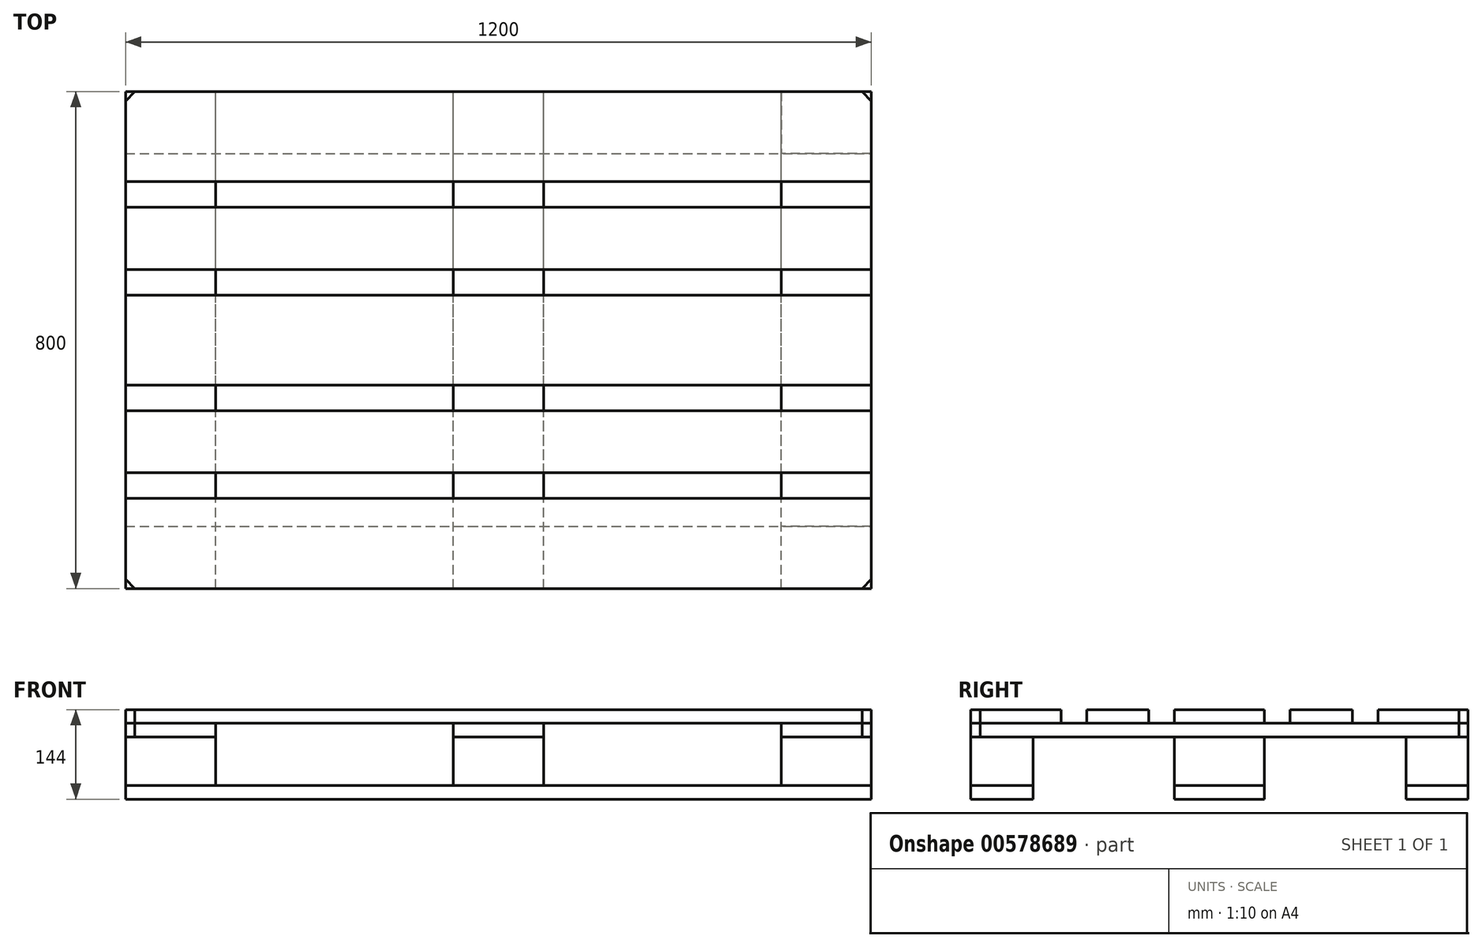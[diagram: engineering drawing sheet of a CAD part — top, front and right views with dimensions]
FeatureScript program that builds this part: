
annotation { "Feature Type Name" : "Feature", "Feature Type Description" : "" }
export const myFeature = defineFeature(function(context is Context, id is Id, definition is map)
    precondition{}
    {
        {
            var Q0;
            Q0=qCreatedBy(makeId("Top.planeOp"),FACE);
            var sketch = newSketch(context, id + "F0", { "sketchPlane" : qUnion([Q0])});
            skLineSegment(sketch, "E0.bottom", {"start": v(600, -72.5) * mm, "end": v(-600, -72.5) * mm});
            skLineSegment(sketch, "E0.top", {"start": v(600, 72.5) * mm, "end": v(-600, 72.5) * mm});
            skLineSegment(sketch, "E0.left", {"start": v(600, -72.5) * mm, "end": v(600, 72.5) * mm});
            skLineSegment(sketch, "E0.right", {"start": v(-600, -72.5) * mm, "end": v(-600, 72.5) * mm});
            skPoint(sketch, "E0.middle", {"position": v(0, 0) * mm});
            skLineSegment(sketch, "E1.bottom", {"start": v(600, -213.75) * mm, "end": v(-600, -213.75) * mm});
            skLineSegment(sketch, "E1.top", {"start": v(600, -113.75) * mm, "end": v(-600, -113.75) * mm});
            skLineSegment(sketch, "E1.left", {"start": v(600, -213.75) * mm, "end": v(600, -113.75) * mm});
            skLineSegment(sketch, "E1.right", {"start": v(-600, -213.75) * mm, "end": v(-600, -113.75) * mm});
            skPoint(sketch, "E1.middle", {"position": v(0, -163.75) * mm});
            skLineSegment(sketch, "E2.bottom", {"start": v(600, -400) * mm, "end": v(-600, -400) * mm});
            skLineSegment(sketch, "E2.top", {"start": v(600, -255) * mm, "end": v(-600, -255) * mm});
            skLineSegment(sketch, "E2.left", {"start": v(600, -400) * mm, "end": v(600, -255) * mm});
            skLineSegment(sketch, "E2.right", {"start": v(-600, -400) * mm, "end": v(-600, -255) * mm});
            skPoint(sketch, "E2.middle", {"position": v(0, -327.5) * mm});
            skLineSegment(sketch, "E3.bottom", {"start": v(-600, 213.75) * mm, "end": v(600, 213.75) * mm});
            skLineSegment(sketch, "E3.top", {"start": v(-600, 113.75) * mm, "end": v(600, 113.75) * mm});
            skLineSegment(sketch, "E3.left", {"start": v(-600, 213.75) * mm, "end": v(-600, 113.75) * mm});
            skLineSegment(sketch, "E3.right", {"start": v(600, 213.75) * mm, "end": v(600, 113.75) * mm});
            skPoint(sketch, "E3.middle", {"position": v(0, 163.75) * mm});
            skLineSegment(sketch, "E4.bottom", {"start": v(-600, 400) * mm, "end": v(600, 400) * mm});
            skLineSegment(sketch, "E4.top", {"start": v(-600, 255) * mm, "end": v(600, 255) * mm});
            skLineSegment(sketch, "E4.left", {"start": v(-600, 400) * mm, "end": v(-600, 255) * mm});
            skLineSegment(sketch, "E4.right", {"start": v(600, 400) * mm, "end": v(600, 255) * mm});
            skPoint(sketch, "E4.middle", {"position": v(0, 327.5) * mm});
            skLineSegment(sketch, "E5", {"start": v(-600, 163.75) * mm, "end": v(600, 163.75) * mm, "construction": true});
            skSolve(sketch);
        }
        {
            var Q0;
            Q0=makeQuery(id+"F0.imprint","IMPRINT",FACE,{"disambiguationData":[TD([[makeQuery(id+"F0.imprint","IMPRINT",EDGE,{"derivedFrom":sQuery(id+"F0.wireOp",EDGE,"E4.bottom")}),-1.0]])]});
            var Q1;
            Q1=makeQuery(id+"F0.imprint","IMPRINT",FACE,{"disambiguationData":[TD([[makeQuery(id+"F0.imprint","IMPRINT",EDGE,{"derivedFrom":sQuery(id+"F0.wireOp",EDGE,"E3.bottom")}),-1.0]])]});
            var Q2;
            Q2=makeQuery(id+"F0.imprint","IMPRINT",FACE,{"disambiguationData":[TD([[makeQuery(id+"F0.imprint","IMPRINT",EDGE,{"derivedFrom":sQuery(id+"F0.wireOp",EDGE,"E0.bottom")}),-1.0]])]});
            var Q3;
            Q3=makeQuery(id+"F0.imprint","IMPRINT",FACE,{"disambiguationData":[TD([[makeQuery(id+"F0.imprint","IMPRINT",EDGE,{"derivedFrom":sQuery(id+"F0.wireOp",EDGE,"E1.bottom")}),-1.0]])]});
            var Q4;
            Q4=makeQuery(id+"F0.imprint","IMPRINT",FACE,{"disambiguationData":[TD([[makeQuery(id+"F0.imprint","IMPRINT",EDGE,{"derivedFrom":sQuery(id+"F0.wireOp",EDGE,"E2.bottom")}),-1.0]])]});
            extrude(context, id + "F1", {"entities" : qUnion([Q0, Q1, Q2, Q3, Q4]), "oppositeDirection" : true, "depth" : 22 * mm, "offsetDistance" : 25 * mm});
        }
        {
            var Q0;
            Q0=makeQuery(id+"F1.opExtrude","CAP_FACE",FACE,{"disambiguationData":[OSD([sQuery(id+"F0.wireOp",EDGE,"E2.bottom"),sQuery(id+"F0.wireOp",EDGE,"E2.top"),sQuery(id+"F0.wireOp",EDGE,"E2.left"),sQuery(id+"F0.wireOp",EDGE,"E2.right")])],"isStart":false});
            var sketch = newSketch(context, id + "F2", { "sketchPlane" : qUnion([Q0])});
            skLineSegment(sketch, "E6.bottom", {"start": v(-600, 400) * mm, "end": v(-455, 400) * mm});
            skLineSegment(sketch, "E6.top", {"start": v(-600, -400) * mm, "end": v(-455, -400) * mm});
            skLineSegment(sketch, "E6.left", {"start": v(-600, 400) * mm, "end": v(-600, -400) * mm});
            skLineSegment(sketch, "E6.right", {"start": v(-455, 400) * mm, "end": v(-455, -400) * mm});
            skLineSegment(sketch, "E7.bottom", {"start": v(-72.5, 400) * mm, "end": v(72.5, 400) * mm});
            skLineSegment(sketch, "E7.top", {"start": v(-72.5, -400) * mm, "end": v(72.5, -400) * mm});
            skLineSegment(sketch, "E7.left", {"start": v(-72.5, 400) * mm, "end": v(-72.5, -400) * mm});
            skLineSegment(sketch, "E7.right", {"start": v(72.5, 400) * mm, "end": v(72.5, -400) * mm});
            skLineSegment(sketch, "E8.bottom", {"start": v(600, 400) * mm, "end": v(455, 400) * mm});
            skLineSegment(sketch, "E8.top", {"start": v(600, -400) * mm, "end": v(455, -400) * mm});
            skLineSegment(sketch, "E8.left", {"start": v(600, 400) * mm, "end": v(600, -400) * mm});
            skLineSegment(sketch, "E8.right", {"start": v(455, 400) * mm, "end": v(455, -400) * mm});
            skSolve(sketch);
        }
        {
            var Q0;
            {var subQ0=sQuery(id+"F2.wireOp",EDGE,"E6.top");Q0=makeQuery(id+"F2.imprint","IMPRINT",FACE,{"disambiguationData":[TD([[makeQuery(id+"F2.imprint","IMPRINT",EDGE,{"derivedFrom":subQ0}),1.0]])]});}
            var Q1;
            {var subQ0=sQuery(id+"F2.wireOp",EDGE,"E6.bottom");Q1=makeQuery(id+"F2.imprint","IMPRINT",FACE,{"disambiguationData":[TD([[makeQuery(id+"F2.imprint","IMPRINT",EDGE,{"derivedFrom":subQ0}),1.0]])]});}
            var Q2;
            {var subQ0=sQuery(id+"F2.wireOp",EDGE,"E7.bottom");Q2=makeQuery(id+"F2.imprint","IMPRINT",FACE,{"disambiguationData":[TD([[makeQuery(id+"F2.imprint","IMPRINT",EDGE,{"derivedFrom":subQ0}),1.0]])]});}
            var Q3;
            {var subQ0=sQuery(id+"F2.wireOp",EDGE,"E7.top");Q3=makeQuery(id+"F2.imprint","IMPRINT",FACE,{"disambiguationData":[TD([[makeQuery(id+"F2.imprint","IMPRINT",EDGE,{"derivedFrom":subQ0}),1.0]])]});}
            var Q4;
            {var subQ0=sQuery(id+"F2.wireOp",EDGE,"E8.bottom");Q4=makeQuery(id+"F2.imprint","IMPRINT",FACE,{"disambiguationData":[TD([[makeQuery(id+"F2.imprint","IMPRINT",EDGE,{"derivedFrom":subQ0}),1.0]])]});}
            var Q5;
            {var subQ0=sQuery(id+"F2.wireOp",EDGE,"E8.top");Q5=makeQuery(id+"F2.imprint","IMPRINT",FACE,{"disambiguationData":[TD([[makeQuery(id+"F2.imprint","IMPRINT",EDGE,{"derivedFrom":subQ0}),-1.0]])]});}
            extrude(context, id + "F3", {"entities" : qUnion([Q0, Q1, Q2, Q3, Q4, Q5]), "depth" : 22 * mm, "offsetDistance" : 25 * mm});
        }
        {
            var Q0;
            Q0=makeQuery(id+"F3.opExtrude","CAP_FACE",FACE,{"disambiguationData":[OSD([sQuery(id+"F2.wireOp",EDGE,"E6.bottom"),sQuery(id+"F2.wireOp",EDGE,"E6.top"),sQuery(id+"F2.wireOp",EDGE,"E6.left"),sQuery(id+"F2.wireOp",EDGE,"E6.right")])],"isStart":false});
            var sketch = newSketch(context, id + "F4", { "sketchPlane" : qUnion([Q0])});
            skLineSegment(sketch, "E9.bottom", {"start": v(-600, -400) * mm, "end": v(-455, -400) * mm});
            skLineSegment(sketch, "E9.top", {"start": v(-600, -300) * mm, "end": v(-455, -300) * mm});
            skLineSegment(sketch, "E9.left", {"start": v(-600, -400) * mm, "end": v(-600, -300) * mm});
            skLineSegment(sketch, "E9.right", {"start": v(-455, -400) * mm, "end": v(-455, -300) * mm});
            skLineSegment(sketch, "E10", {"start": v(-600, 0) * mm, "end": v(600, 0) * mm, "construction": true});
            skPoint(sketch, "E10.endSnap0", {"position": v(-600, 0) * mm});
            skLineSegment(sketch, "E11", {"start": v(0, 0) * mm, "end": v(0, 291.88) * mm, "construction": true});
            skLineSegment(sketch, "E12.MirrorCS", {"start": v(-600, 300) * mm, "end": v(-455, 300) * mm});
            skLineSegment(sketch, "E13.MirrorCS", {"start": v(-455, 400) * mm, "end": v(-455, 300) * mm});
            skLineSegment(sketch, "E14.MirrorCS", {"start": v(-600, 400) * mm, "end": v(-455, 400) * mm});
            skLineSegment(sketch, "E15.MirrorCS", {"start": v(-600, 400) * mm, "end": v(-600, 300) * mm});
            skLineSegment(sketch, "E16.bottom", {"start": v(-600, -72.5) * mm, "end": v(-455, -72.5) * mm});
            skLineSegment(sketch, "E16.top", {"start": v(-600, 72.5) * mm, "end": v(-455, 72.5) * mm});
            skLineSegment(sketch, "E16.left", {"start": v(-600, -72.5) * mm, "end": v(-600, 72.5) * mm});
            skLineSegment(sketch, "E16.right", {"start": v(-455, -72.5) * mm, "end": v(-455, 72.5) * mm});
            skPoint(sketch, "E17.MirrorP", {"position": v(600, 0) * mm});
            skLineSegment(sketch, "E18.MirrorCS", {"start": v(455, -72.5) * mm, "end": v(455, 72.5) * mm});
            skLineSegment(sketch, "E19.MirrorCS", {"start": v(600, -400) * mm, "end": v(455, -400) * mm});
            skLineSegment(sketch, "E20.MirrorCS", {"start": v(600, 400) * mm, "end": v(455, 400) * mm});
            skLineSegment(sketch, "E21.MirrorCS", {"start": v(600, -400) * mm, "end": v(600, -300) * mm});
            skLineSegment(sketch, "E22.MirrorCS", {"start": v(455, 400) * mm, "end": v(455, 300) * mm});
            skLineSegment(sketch, "E23.MirrorCS", {"start": v(600, -72.5) * mm, "end": v(455, -72.5) * mm});
            skLineSegment(sketch, "E24.MirrorCS", {"start": v(455, -400) * mm, "end": v(455, -300) * mm});
            skLineSegment(sketch, "E25.MirrorCS", {"start": v(600, 72.5) * mm, "end": v(455, 72.5) * mm});
            skLineSegment(sketch, "E26.MirrorCS", {"start": v(600, 400) * mm, "end": v(600, 300) * mm});
            skLineSegment(sketch, "E27.MirrorCS", {"start": v(600, -72.5) * mm, "end": v(600, 72.5) * mm});
            skLineSegment(sketch, "E28.MirrorCS", {"start": v(600, -300) * mm, "end": v(455, -300) * mm});
            skLineSegment(sketch, "E29.MirrorCS", {"start": v(600, 300) * mm, "end": v(455, 300) * mm});
            skPoint(sketch, "E30", {"position": v(0, 0) * mm});
            skSolve(sketch);
        }
        {
            var Q0;
            Q0=makeQuery(id+"F3.opExtrude","CAP_FACE",FACE,{"disambiguationData":[OSD([sQuery(id+"F2.wireOp",EDGE,"E7.bottom"),sQuery(id+"F2.wireOp",EDGE,"E7.top"),sQuery(id+"F2.wireOp",EDGE,"E7.left"),sQuery(id+"F2.wireOp",EDGE,"E7.right")])],"isStart":false});
            var sketch = newSketch(context, id + "F5", { "sketchPlane" : qUnion([Q0])});
            skLineSegment(sketch, "E31.bottom", {"start": v(-72.5, -400) * mm, "end": v(72.5, -400) * mm});
            skLineSegment(sketch, "E31.top", {"start": v(-72.5, -300) * mm, "end": v(72.5, -300) * mm});
            skLineSegment(sketch, "E31.left", {"start": v(-72.5, -400) * mm, "end": v(-72.5, -300) * mm});
            skLineSegment(sketch, "E31.right", {"start": v(72.5, -400) * mm, "end": v(72.5, -300) * mm});
            skLineSegment(sketch, "E32.bottom", {"start": v(-72.5, 400) * mm, "end": v(72.5, 400) * mm});
            skLineSegment(sketch, "E32.top", {"start": v(-72.5, 300) * mm, "end": v(72.5, 300) * mm});
            skLineSegment(sketch, "E32.left", {"start": v(-72.5, 400) * mm, "end": v(-72.5, 300) * mm});
            skLineSegment(sketch, "E32.right", {"start": v(72.5, 400) * mm, "end": v(72.5, 300) * mm});
            skLineSegment(sketch, "E33.bottom", {"start": v(-72.5, 72.5) * mm, "end": v(72.5, 72.5) * mm});
            skLineSegment(sketch, "E33.top", {"start": v(-72.5, -72.5) * mm, "end": v(72.5, -72.5) * mm});
            skLineSegment(sketch, "E33.left", {"start": v(-72.5, 72.5) * mm, "end": v(-72.5, -72.5) * mm});
            skLineSegment(sketch, "E33.right", {"start": v(72.5, 72.5) * mm, "end": v(72.5, -72.5) * mm});
            skPoint(sketch, "E34", {"position": v(-72.5, 0) * mm});
            skSolve(sketch);
        }
        {
            var Q0;
            Q0=makeQuery(id+"FYTJBSPpSRuX8gd_8.imprint","IMPRINT",FACE,{"disambiguationData":[TD([[makeQuery(id+"FYTJBSPpSRuX8gd_8.imprint","IMPRINT",EDGE,{"derivedFrom":sQuery(id+"FYTJBSPpSRuX8gd_8.wireOp",EDGE,"gy2sHMVN-xgZd-mj2R-ffUc-dkCIv1PvmpuS.bottom")}),1.0]])]});
            var Q1;
            Q1=makeQuery(id+"FYTJBSPpSRuX8gd_8.imprint","IMPRINT",FACE,{"disambiguationData":[TD([[makeQuery(id+"FYTJBSPpSRuX8gd_8.imprint","IMPRINT",EDGE,{"derivedFrom":sQuery(id+"FYTJBSPpSRuX8gd_8.wireOp",EDGE,"vENXevhf-lpDf-Ta8S-9Xc3-8ZelHCq2notW.bottom")}),-1.0]])]});
            var Q2;
            Q2=makeQuery(id+"FYTJBSPpSRuX8gd_8.imprint","IMPRINT",FACE,{"disambiguationData":[TD([[makeQuery(id+"FYTJBSPpSRuX8gd_8.imprint","IMPRINT",EDGE,{"derivedFrom":sQuery(id+"FYTJBSPpSRuX8gd_8.wireOp",EDGE,"zKUPhiTK-GL8t-0yBU-HGnA-DaKmiHeKaOVc.bottom")}),1.0]])]});
            var Q3;
            Q3=makeQuery(id+"FYTJBSPpSRuX8gd_8.imprint","IMPRINT",FACE,{"disambiguationData":[TD([[makeQuery(id+"FYTJBSPpSRuX8gd_8.imprint","IMPRINT",EDGE,{"derivedFrom":sQuery(id+"FYTJBSPpSRuX8gd_8.wireOp",EDGE,"ad5ac969-15a0-44eb-bdcf-7e8a1a59a2c6.1.0.7")}),1.0]])]});
            var Q4;
            Q4=makeQuery(id+"FYTJBSPpSRuX8gd_8.imprint","IMPRINT",FACE,{"disambiguationData":[TD([[makeQuery(id+"FYTJBSPpSRuX8gd_8.imprint","IMPRINT",EDGE,{"derivedFrom":sQuery(id+"FYTJBSPpSRuX8gd_8.wireOp",EDGE,"ad5ac969-15a0-44eb-bdcf-7e8a1a59a2c6.1.0.0")}),1.0]])]});
            var Q5;
            Q5=makeQuery(id+"FYTJBSPpSRuX8gd_8.imprint","IMPRINT",FACE,{"disambiguationData":[TD([[makeQuery(id+"FYTJBSPpSRuX8gd_8.imprint","IMPRINT",EDGE,{"derivedFrom":sQuery(id+"FYTJBSPpSRuX8gd_8.wireOp",EDGE,"ad5ac969-15a0-44eb-bdcf-7e8a1a59a2c6.1.0.3")}),-1.0]])]});
            var Q6;
            Q6=makeQuery(id+"FYTJBSPpSRuX8gd_8.imprint","IMPRINT",FACE,{"disambiguationData":[TD([[makeQuery(id+"FYTJBSPpSRuX8gd_8.imprint","IMPRINT",EDGE,{"derivedFrom":sQuery(id+"FYTJBSPpSRuX8gd_8.wireOp",EDGE,"ad5ac969-15a0-44eb-bdcf-7e8a1a59a2c6.2.0.3")}),-1.0]])]});
            var Q7;
            Q7=makeQuery(id+"FYTJBSPpSRuX8gd_8.imprint","IMPRINT",FACE,{"disambiguationData":[TD([[makeQuery(id+"FYTJBSPpSRuX8gd_8.imprint","IMPRINT",EDGE,{"derivedFrom":sQuery(id+"FYTJBSPpSRuX8gd_8.wireOp",EDGE,"ad5ac969-15a0-44eb-bdcf-7e8a1a59a2c6.2.0.0")}),1.0]])]});
            var Q8;
            Q8=makeQuery(id+"FYTJBSPpSRuX8gd_8.imprint","IMPRINT",FACE,{"disambiguationData":[TD([[makeQuery(id+"FYTJBSPpSRuX8gd_8.imprint","IMPRINT",EDGE,{"derivedFrom":sQuery(id+"FYTJBSPpSRuX8gd_8.wireOp",EDGE,"ad5ac969-15a0-44eb-bdcf-7e8a1a59a2c6.2.0.7")}),1.0]])]});
            var Q9;
            Q9=makeQuery(id+"F4.imprint","IMPRINT",FACE,{"disambiguationData":[TD([[makeQuery(id+"F4.imprint","IMPRINT",EDGE,{"derivedFrom":sQuery(id+"F4.wireOp",EDGE,"E9.bottom")}),1.0]])]});
            var Q10;
            Q10=makeQuery(id+"F4.imprint","IMPRINT",FACE,{"disambiguationData":[TD([[makeQuery(id+"F4.imprint","IMPRINT",EDGE,{"derivedFrom":sQuery(id+"F4.wireOp",EDGE,"E12.MirrorCS")}),1.0]])]});
            var Q11;
            Q11=makeQuery(id+"F4.imprint","IMPRINT",FACE,{"disambiguationData":[TD([[makeQuery(id+"F4.imprint","IMPRINT",EDGE,{"derivedFrom":sQuery(id+"F4.wireOp",EDGE,"E19.MirrorCS")}),-1.0]])]});
            var Q12;
            Q12=makeQuery(id+"F4.imprint","IMPRINT",FACE,{"disambiguationData":[TD([[makeQuery(id+"F4.imprint","IMPRINT",EDGE,{"derivedFrom":sQuery(id+"F4.wireOp",EDGE,"E18.MirrorCS")}),-1.0]])]});
            var Q13;
            Q13=makeQuery(id+"F4.imprint","IMPRINT",FACE,{"disambiguationData":[TD([[makeQuery(id+"F4.imprint","IMPRINT",EDGE,{"derivedFrom":sQuery(id+"F4.wireOp",EDGE,"E20.MirrorCS")}),1.0]])]});
            var Q14;
            Q14=makeQuery(id+"F4.imprint","IMPRINT",FACE,{"disambiguationData":[TD([[makeQuery(id+"F4.imprint","IMPRINT",EDGE,{"derivedFrom":sQuery(id+"F4.wireOp",EDGE,"E16.bottom")}),1.0]])]});
            var Q15;
            Q15=makeQuery(id+"F5.imprint","IMPRINT",FACE,{"disambiguationData":[TD([[makeQuery(id+"F5.imprint","IMPRINT",EDGE,{"derivedFrom":sQuery(id+"F5.wireOp",EDGE,"E33.bottom")}),-1.0]])]});
            var Q16;
            Q16=makeQuery(id+"F5.imprint","IMPRINT",FACE,{"disambiguationData":[TD([[makeQuery(id+"F5.imprint","IMPRINT",EDGE,{"derivedFrom":sQuery(id+"F5.wireOp",EDGE,"E32.bottom")}),1.0]])]});
            var Q17;
            Q17=makeQuery(id+"F5.imprint","IMPRINT",FACE,{"disambiguationData":[TD([[makeQuery(id+"F5.imprint","IMPRINT",EDGE,{"derivedFrom":sQuery(id+"F5.wireOp",EDGE,"E31.bottom")}),1.0]])]});
            extrude(context, id + "F6", {"entities" : qUnion([Q0, Q1, Q2, Q3, Q4, Q5, Q6, Q7, Q8, Q9, Q10, Q11, Q12, Q13, Q14, Q15, Q16, Q17]), "depth" : 78 * mm, "offsetDistance" : 25 * mm});
        }
        {
            var Q0;
            Q0=makeQuery(id+"F6.opExtrude","CAP_FACE",FACE,{"disambiguationData":[OSD([sQuery(id+"F4.wireOp",EDGE,"E9.bottom"),sQuery(id+"F4.wireOp",EDGE,"E9.top"),sQuery(id+"F4.wireOp",EDGE,"E9.left"),sQuery(id+"F4.wireOp",EDGE,"E9.right")])],"isStart":false});
            var sketch = newSketch(context, id + "F7", { "sketchPlane" : qUnion([Q0])});
            skLineSegment(sketch, "E35.bottom", {"start": v(-600, -400) * mm, "end": v(600, -400) * mm});
            skLineSegment(sketch, "E35.top", {"start": v(-600, -300) * mm, "end": v(600, -300) * mm});
            skLineSegment(sketch, "E35.left", {"start": v(-600, -400) * mm, "end": v(-600, -300) * mm});
            skLineSegment(sketch, "E35.right", {"start": v(600, -400) * mm, "end": v(600, -300) * mm});
            skLineSegment(sketch, "E36.bottom", {"start": v(-600, -72.5) * mm, "end": v(600, -72.5) * mm});
            skLineSegment(sketch, "E36.top", {"start": v(-600, 72.5) * mm, "end": v(600, 72.5) * mm});
            skLineSegment(sketch, "E36.left", {"start": v(-600, -72.5) * mm, "end": v(-600, 72.5) * mm});
            skLineSegment(sketch, "E36.right", {"start": v(600, -72.5) * mm, "end": v(600, 72.5) * mm});
            skLineSegment(sketch, "E37.bottom", {"start": v(-600, 300) * mm, "end": v(600, 300) * mm});
            skLineSegment(sketch, "E37.top", {"start": v(-600, 400) * mm, "end": v(600, 400) * mm});
            skLineSegment(sketch, "E37.left", {"start": v(-600, 300) * mm, "end": v(-600, 400) * mm});
            skLineSegment(sketch, "E37.right", {"start": v(600, 300) * mm, "end": v(600, 400) * mm});
            skSolve(sketch);
        }
        {
            var Q0;
            {var subQ0=sQuery(id+"F7.wireOp",EDGE,"E35.left");Q0=makeQuery(id+"F7.imprint","IMPRINT",FACE,{"disambiguationData":[TD([[makeQuery(id+"F7.imprint","IMPRINT",EDGE,{"derivedFrom":subQ0}),1.0]])]});}
            var Q1;
            {var subQ2=sQuery(id+"F7.wireOp",EDGE,"E35.right");Q1=makeQuery(id+"F7.imprint","IMPRINT",FACE,{"disambiguationData":[TD([[makeQuery(id+"F7.imprint","IMPRINT",EDGE,{"derivedFrom":subQ2}),1.0]])]});}
            var Q2;
            Q2=makeQuery(id+"F7.imprint","IMPRINT",FACE,{"disambiguationData":[TD([[makeQuery(id+"F7.imprint","IMPRINT",EDGE,{"derivedFrom":sQuery(id+"F7.wireOp",EDGE,"E36.bottom")}),1.0]])]});
            var Q3;
            Q3=makeQuery(id+"F7.imprint","IMPRINT",FACE,{"disambiguationData":[TD([[makeQuery(id+"F7.imprint","IMPRINT",EDGE,{"derivedFrom":sQuery(id+"F7.wireOp",EDGE,"E37.bottom")}),1.0]])]});
            extrude(context, id + "F8", {"entities" : qUnion([Q0, Q1, Q2, Q3]), "depth" : 22 * mm, "offsetDistance" : 25 * mm});
        }
        {
            var Q0;
            Q0=makeQuery(id+"F1.opExtrude","SWEPT_EDGE",EDGE,{"disambiguationData":[OSD([sQuery(id+"F0.wireOp",EDGE,"E2.bottom"),sQuery(id+"F0.wireOp",EDGE,"E2.right")])]});
            var Q1;
            Q1=makeQuery(id+"F3.opExtrude","SWEPT_EDGE",EDGE,{"disambiguationData":[OSD([sQuery(id+"F2.wireOp",EDGE,"E6.bottom"),sQuery(id+"F2.wireOp",EDGE,"E6.left")])]});
            var Q2;
            Q2=makeQuery(id+"F6.opExtrude","SWEPT_EDGE",EDGE,{"disambiguationData":[OSD([sQuery(id+"FYTJBSPpSRuX8gd_8.wireOp",EDGE,"gy2sHMVN-xgZd-mj2R-ffUc-dkCIv1PvmpuS.bottom"),sQuery(id+"FYTJBSPpSRuX8gd_8.wireOp",EDGE,"gy2sHMVN-xgZd-mj2R-ffUc-dkCIv1PvmpuS.left")])]});
            var Q3;
            Q3=makeQuery(id+"F8.opExtrude","SWEPT_EDGE",EDGE,{"disambiguationData":[OSD([sQuery(id+"FUbmOA5CFNu3vIk_17.wireOp",EDGE,"HQ4nohft-M4JY-dTNH-rdQb-ztwkA5vyvlAQ.bottom"),sQuery(id+"FUbmOA5CFNu3vIk_17.wireOp",EDGE,"HQ4nohft-M4JY-dTNH-rdQb-ztwkA5vyvlAQ.left")])]});
            var Q4;
            Q4=makeQuery(id+"F1.opExtrude","SWEPT_EDGE",EDGE,{"disambiguationData":[OSD([sQuery(id+"F0.wireOp",EDGE,"E2.bottom"),sQuery(id+"F0.wireOp",EDGE,"E2.left")])]});
            var Q5;
            Q5=makeQuery(id+"F3.opExtrude","SWEPT_EDGE",EDGE,{"disambiguationData":[OSD([sQuery(id+"F2.wireOp",EDGE,"E8.bottom"),sQuery(id+"F2.wireOp",EDGE,"E8.left")])]});
            var Q6;
            Q6=makeQuery(id+"F6.opExtrude","SWEPT_EDGE",EDGE,{"disambiguationData":[OSD([sQuery(id+"FYTJBSPpSRuX8gd_8.wireOp",EDGE,"ad5ac969-15a0-44eb-bdcf-7e8a1a59a2c6.2.0.3"),sQuery(id+"FYTJBSPpSRuX8gd_8.wireOp",EDGE,"ad5ac969-15a0-44eb-bdcf-7e8a1a59a2c6.2.0.8")])]});
            var Q7;
            Q7=makeQuery(id+"F8.opExtrude","SWEPT_EDGE",EDGE,{"disambiguationData":[OSD([sQuery(id+"FUbmOA5CFNu3vIk_17.wireOp",EDGE,"HQ4nohft-M4JY-dTNH-rdQb-ztwkA5vyvlAQ.bottom"),sQuery(id+"FUbmOA5CFNu3vIk_17.wireOp",EDGE,"HQ4nohft-M4JY-dTNH-rdQb-ztwkA5vyvlAQ.right")])]});
            var Q8;
            Q8=makeQuery(id+"F1.opExtrude","SWEPT_EDGE",EDGE,{"disambiguationData":[OSD([sQuery(id+"F0.wireOp",EDGE,"E4.bottom"),sQuery(id+"F0.wireOp",EDGE,"E4.right")])]});
            var Q9;
            Q9=makeQuery(id+"F3.opExtrude","SWEPT_EDGE",EDGE,{"disambiguationData":[OSD([sQuery(id+"F2.wireOp",EDGE,"E8.top"),sQuery(id+"F2.wireOp",EDGE,"E8.left")])]});
            var Q10;
            Q10=makeQuery(id+"F6.opExtrude","SWEPT_EDGE",EDGE,{"disambiguationData":[OSD([sQuery(id+"FYTJBSPpSRuX8gd_8.wireOp",EDGE,"ad5ac969-15a0-44eb-bdcf-7e8a1a59a2c6.2.0.7"),sQuery(id+"FYTJBSPpSRuX8gd_8.wireOp",EDGE,"ad5ac969-15a0-44eb-bdcf-7e8a1a59a2c6.2.0.9")])]});
            var Q11;
            Q11=makeQuery(id+"F8.opExtrude","SWEPT_EDGE",EDGE,{"disambiguationData":[OSD([sQuery(id+"FUbmOA5CFNu3vIk_17.wireOp",EDGE,"4kciwtxH-OBSt-f0dC-ou1O-WIhG8iqRsqLm.top"),sQuery(id+"FUbmOA5CFNu3vIk_17.wireOp",EDGE,"4kciwtxH-OBSt-f0dC-ou1O-WIhG8iqRsqLm.right")])]});
            var Q12;
            Q12=makeQuery(id+"F1.opExtrude","SWEPT_EDGE",EDGE,{"disambiguationData":[OSD([sQuery(id+"F0.wireOp",EDGE,"E4.bottom"),sQuery(id+"F0.wireOp",EDGE,"E4.left")])]});
            var Q13;
            Q13=makeQuery(id+"F3.opExtrude","SWEPT_EDGE",EDGE,{"disambiguationData":[OSD([sQuery(id+"F2.wireOp",EDGE,"E6.top"),sQuery(id+"F2.wireOp",EDGE,"E6.left")])]});
            var Q14;
            Q14=makeQuery(id+"F6.opExtrude","SWEPT_EDGE",EDGE,{"disambiguationData":[OSD([sQuery(id+"FYTJBSPpSRuX8gd_8.wireOp",EDGE,"zKUPhiTK-GL8t-0yBU-HGnA-DaKmiHeKaOVc.bottom"),sQuery(id+"FYTJBSPpSRuX8gd_8.wireOp",EDGE,"zKUPhiTK-GL8t-0yBU-HGnA-DaKmiHeKaOVc.left")])]});
            var Q15;
            Q15=makeQuery(id+"F8.opExtrude","SWEPT_EDGE",EDGE,{"disambiguationData":[OSD([sQuery(id+"FUbmOA5CFNu3vIk_17.wireOp",EDGE,"4kciwtxH-OBSt-f0dC-ou1O-WIhG8iqRsqLm.top"),sQuery(id+"FUbmOA5CFNu3vIk_17.wireOp",EDGE,"4kciwtxH-OBSt-f0dC-ou1O-WIhG8iqRsqLm.left")])]});
            chamfer(context, id + "F9", {"entities" : qUnion([Q0, Q1, Q2, Q3, Q4, Q5, Q6, Q7, Q8, Q9, Q10, Q11, Q12, Q13, Q14, Q15]), "width" : 15 * mm, "tangentPropagation" : true});
        }
    });
